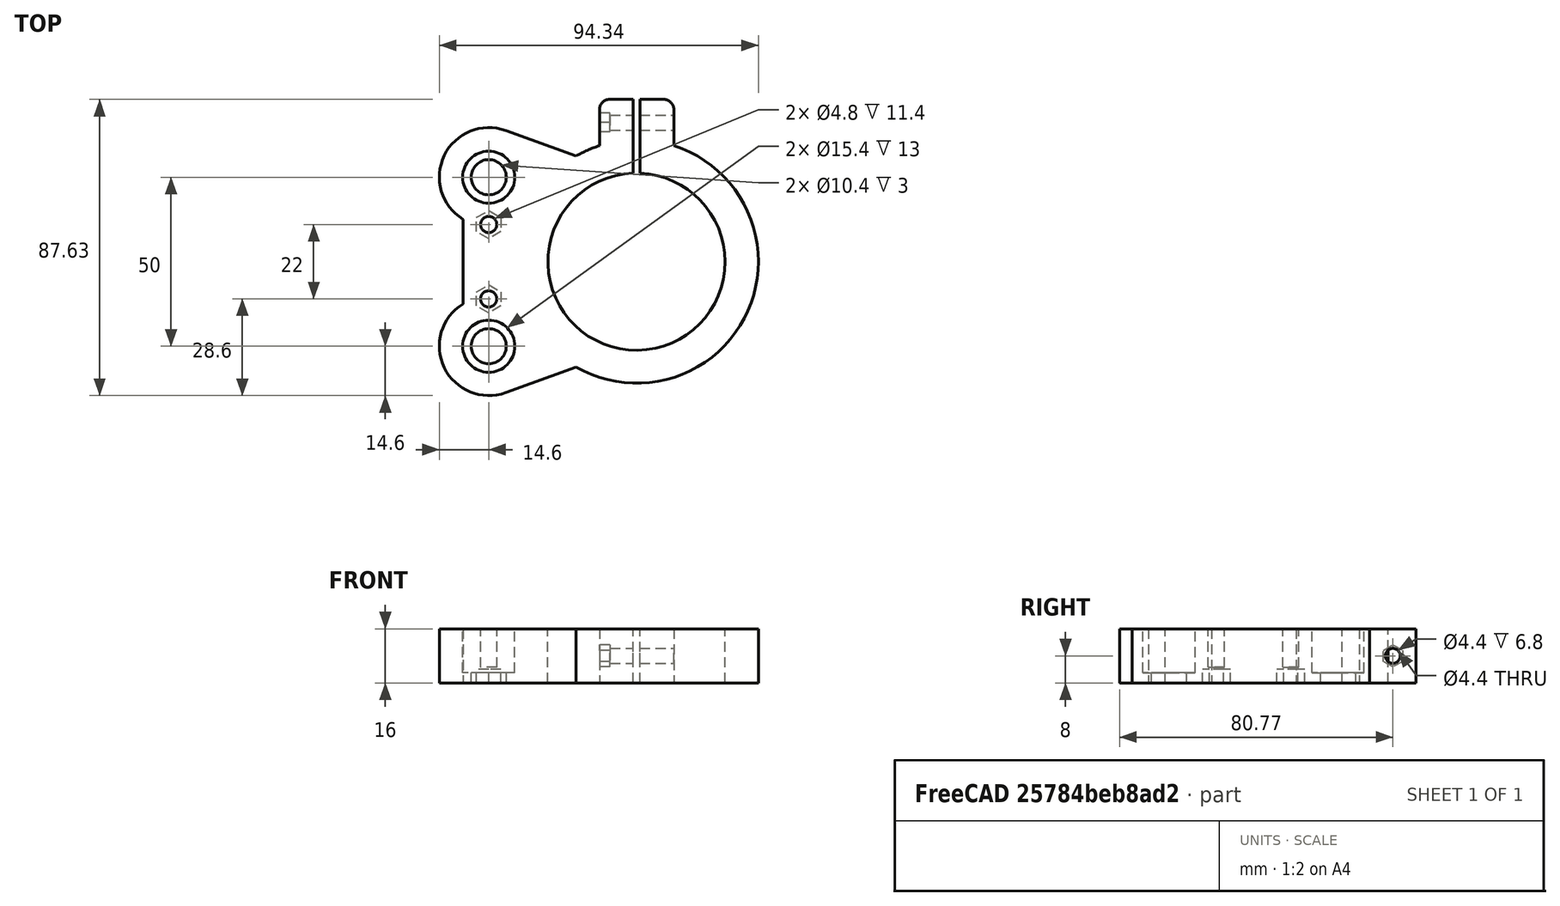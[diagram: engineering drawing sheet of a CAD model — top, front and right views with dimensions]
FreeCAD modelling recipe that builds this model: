
FCSTD DOCUMENT  (FreeCAD 0.15R4664 (Git))
Label: z_spindle_holder
License: All rights reserved
LicenseURL: http://en.wikipedia.org/wiki/All_rights_reserved
objects: Part::Cylinder×8, Part::Cut×8, Part::MultiFuse×4, Part::Prism×3, Part::Feature×2, Mesh::Feature×1, Sketcher::SketchObject×1, PartDesign::Pad×1, Part::Box×1, Part::Fillet×1
note: 30 computed .brp shape members not serialized (recipe doc carries the construction recipe); baked Part::Feature solids carry a one-line shape summary decoded from their .brp

FEATURE [Mesh::Feature] spindleholderantibacklash
FEATURE [Part::Feature] spindleholderantibacklash001001  label="spindleholderantibacklash002"
  shape: bbox 94.34 x 87.63 x 16 mm, 1291 faces, 0 solids (baked)
FEATURE [Sketcher::SketchObject] Sketch
  ExternalGeometry = -> [spindleholderantibacklash001001]
  Placement = pos=(0,0,16) rot=(1,0,0;3.14159rad)
  Support = -> spindleholderantibacklash001001 [Face5]
  sketch-geometry (10):
    g0: ArcOfCircle CenterX=14.6467 CenterY=-64.6499 CenterZ=0 NormalX=0 NormalY=0 NormalZ=1 Radius=14.65 StartAngle=2.12021 EndAngle=5.06145
    g1: ArcOfCircle CenterX=14.6467 CenterY=-14.6499 CenterZ=0 NormalX=0 NormalY=0 NormalZ=1 Radius=14.65 StartAngle=1.22173 EndAngle=4.16298
    g2: ArcOfCircle CenterX=58.3467 CenterY=-39.6499 CenterZ=0 NormalX=0 NormalY=0 NormalZ=1 Radius=35.9947 StartAngle=5.02296 EndAngle=8.37543
    g3: ArcOfCircle CenterX=58.3469 CenterY=-39.6492 CenterZ=0 NormalX=0 NormalY=0 NormalZ=1 Radius=35.9954 StartAngle=4.19094 EndAngle=4.40182
    g4: LineSegment StartX=40.4163 StartY=-70.8607 StartZ=0 EndX=19.6573 EndY=-78.4164 EndZ=0
    g5: LineSegment StartX=6.99666 StartY=-27.1439 StartZ=0 EndX=6.99666 EndY=-52.1559 EndZ=0
    g6: LineSegment StartX=19.6573 StartY=-0.883396 StartZ=0 EndX=40.4163 EndY=-8.43906 EndZ=0
    g7: LineSegment StartX=47.3466 StartY=-73.9226 StartZ=0 EndX=47.3466 EndY=-87.6307 EndZ=0
    g8: LineSegment StartX=69.3466 StartY=-73.9226 StartZ=0 EndX=69.3466 EndY=-87.6307 EndZ=0
    g9: LineSegment StartX=47.3466 StartY=-87.6307 StartZ=0 EndX=69.3466 EndY=-87.6307 EndZ=0
  constraints (26):
    c: Coincident(g0,g-3)
    c: Coincident(g0,g-4)
    c: PointOnObject(g-5,g0)
    c: Coincident(g1,g-4)
    c: Coincident(g1,g-13)
    c: PointOnObject(g-14,g1)
    c: Coincident(g2,g-13)
    c: Coincident(g2,g-10)
    c: PointOnObject(g-12,g2)
    c: Coincident(g3,g-3)
    c: Coincident(g3,g-6)
    c: PointOnObject(g-7,g3)
    c: Coincident(g4,g3)
    c: Coincident(g4,g0)
    c: Coincident(g5,g1)
    c: Coincident(g5,g0)
    c: Coincident(g6,g1)
    c: Coincident(g6,g2)
    c: Coincident(g7,g3)
    c: Vertical(g7)
    c: Coincident(g8,g2)
    c: Vertical(g8)
    c: Horizontal(g9)
    c: PointOnObject(g-8,g9)
    c: Coincident(g9,g7)
    c: Coincident(g8,g9)
FEATURE [Part::Cylinder] Cylinder  label="Cilindro"
  Angle = 360
  Height = 17
  Placement = pos=(14.6,14.6,3) rot=(0,0,1;0rad)
  Radius = 7.7
FEATURE [Part::Cylinder] Cylinder001  label="Cilindro001"
  Angle = 360
  Height = 17
  Placement = pos=(14.6,64.6,3) rot=(0,0,1;0rad)
  Radius = 7.7
FEATURE [Part::MultiFuse] Fusion  label="bearing_holes"
  Shapes = -> [Cylinder,Cylinder001]
FEATURE [Part::Cylinder] Cylinder002  label="Cilindro002"
  Angle = 360
  Height = 13
  Placement = pos=(14.6,28.6,4.6) rot=(0,0,1;0rad)
  Radius = 2.4
FEATURE [Part::Cylinder] Cylinder003  label="Cilindro003"
  Angle = 360
  Height = 13
  Placement = pos=(14.6,50.6,4.6) rot=(0,0,1;0rad)
  Radius = 2.4
FEATURE [Part::MultiFuse] Fusion001  label="screw_holes"
  Shapes = -> [Cylinder002,Cylinder003]
FEATURE [Part::Prism] Prism  label="Prisma"
  Circumradius = 4.15692
  Height = 5
  Placement = pos=(14.6,28.6,-1) rot=(0,0,1;0.523599rad)
  Polygon = 6
FEATURE [Part::Prism] Prism001  label="Prisma001"
  Circumradius = 4.15692
  Height = 5
  Placement = pos=(14.6,50.6,-1) rot=(0,0,1;0.523599rad)
  Polygon = 6
FEATURE [Part::MultiFuse] Fusion002  label="nut_holes"
  Shapes = -> [Prism,Prism001]
FEATURE [Part::Cylinder] Cylinder004  label="Cilindro004"
  Angle = 360
  Height = 17
  Placement = pos=(14.6,14.6,-1) rot=(0,0,1;0rad)
  Radius = 5.2
FEATURE [Part::Cylinder] Cylinder005  label="Cilindro005"
  Angle = 360
  Height = 17
  Placement = pos=(14.6,64.6,-1) rot=(0,0,1;0rad)
  Radius = 5.2
FEATURE [Part::MultiFuse] Fusion003  label="bearing_holes001"
  Shapes = -> [Cylinder004,Cylinder005]
FEATURE [PartDesign::Pad] Pad
  Length = 16
  Length2 = 100
  Sketch = -> Sketch
  Type = 0
FEATURE [Part::Cut] Cut
  Base = -> Pad
  Tool = -> Fusion
FEATURE [Part::Cut] Cut001
  Base = -> Cut
  Tool = -> Fusion002
FEATURE [Part::Cut] Cut002
  Base = -> Cut001
  Tool = -> Fusion001
FEATURE [Part::Cut] Cut003
  Base = -> Cut002
  Tool = -> Fusion003
FEATURE [Part::Cylinder] Cylinder006  label="Cilindro006"
  Angle = 360
  Height = 18
  Placement = pos=(58.3,39.6,-1) rot=(0,0,1;0rad)
  Radius = 26.2
FEATURE [Part::Cut] Cut004
  Base = -> Cut003
  Tool = -> Cylinder006
FEATURE [Part::Box] Box  label="Cubo"
  Height = 18
  Length = 2
  Placement = pos=(57.3,63,-1) rot=(0,0,1;0rad)
  Width = 27
FEATURE [Part::Cut] Cut005
  Base = -> Cut004
  Tool = -> Box
FEATURE [Part::Cylinder] Cylinder007  label="Cilindro007"
  Angle = 360
  Height = 20
  Placement = pos=(50,80.77,8) rot=(0,1,0;1.5708rad)
  Radius = 2.2
FEATURE [Part::Cut] Cut006
  Base = -> Cut005
  Tool = -> Cylinder007
FEATURE [Part::Prism] Prism002  label="Prisma002"
  Circumradius = 3.29
  Height = 4
  Placement = pos=(50.5,80.8,8) rot=(0,-1,0;1.5708rad)
  Polygon = 6
FEATURE [Part::Cut] Cut007
  Base = -> Cut006
  Tool = -> Prism002
FEATURE [Part::Fillet] Fillet
  Base = -> Cut007
  Edges = 2 edges r=3: [Edge57,Edge70]
FEATURE [Part::Feature] Fillet_solid  label="Fillet (Solid)"
  shape: bbox 94.34 x 87.63 x 16 mm, 51 faces (baked)
